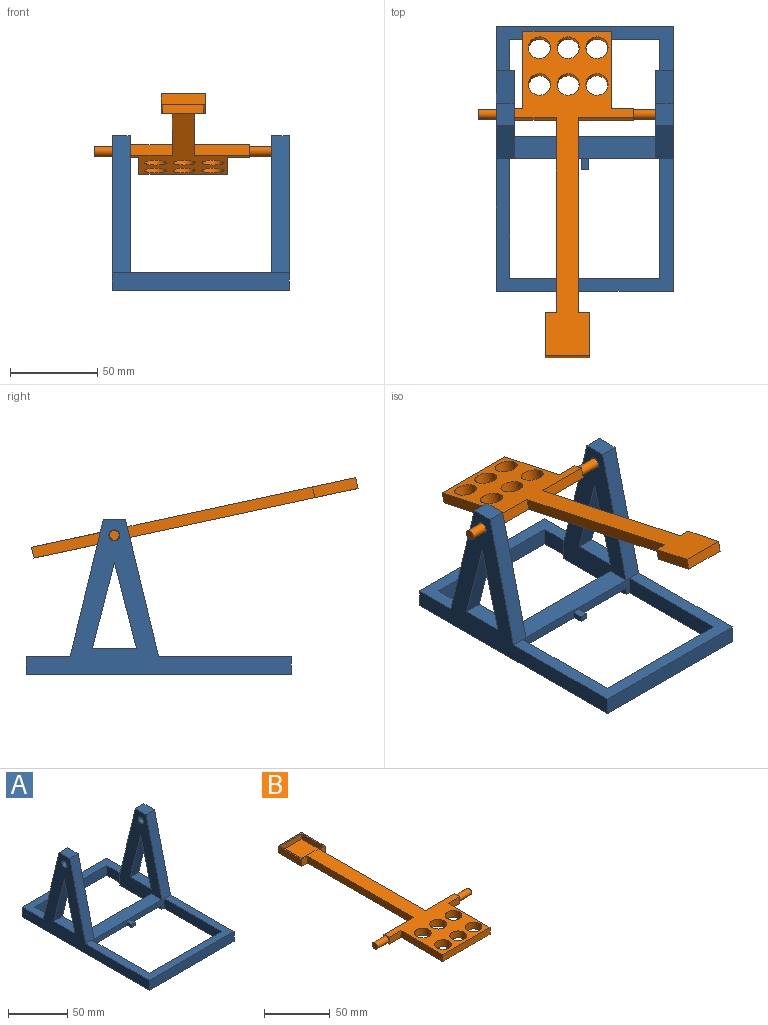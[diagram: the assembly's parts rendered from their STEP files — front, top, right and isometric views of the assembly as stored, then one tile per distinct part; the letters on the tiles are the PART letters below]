
ASSEMBLY  parts=2 mates=1
PART A: 40 faces, bbox 101.6x152.4x88.9 mm
  f0: plane 88.9x50.8mm, normal (-1,0,0), area 2281.3mm2, adj f2,f4,f13,f19,f26,f27,f28,f29
  f1: plane 12.7x10.16mm, normal (0,0,1), area 129mm2, adj f5,f7,f24,f25
  f2: plane 12.7x10.16mm, normal (0,0,1), area 129mm2, adj f0,f6,f30,f31
  f3: plane 10.16x2.54mm, normal (0,1,0), area 25.8mm2, adj f7,f10,f19,f24
  f4: plane 86.36x10.16mm, normal (0,-1,0), area 495.1mm2, adj f0,f7,f14,f16,f19,f25,f31,f32
  f5: plane 152.4x88.9mm, normal (-1,0,0), area 3385.4mm2, adj f1,f8,f9,f17,f18,f19,f20,f21
  f6: plane 152.4x88.9mm, normal (1,0,0), area 3385.4mm2, adj f2,f8,f9,f17,f18,f19,f26,f27
  f7: plane 88.9x50.8mm, normal (1,0,0), area 2281.3mm2, adj f1,f3,f4,f19,f20,f21,f22,f23
  f8: plane 101.6x25.4mm, normal (0,0,1), area 1045.2mm2, adj f5,f6,f10,f11,f12,f17,f24,f30
  f9: plane 101.6x10.16mm, normal (0,-1,0), area 1032.3mm2, adj f5,f6,f18,f19
  f10: plane 17.78x10.16mm, normal (1,0,0), area 180.6mm2, adj f3,f8,f11,f19
  f11: plane 86.36x10.16mm, normal (0,-1,0), area 877.4mm2, adj f8,f10,f12,f19
  f12: plane 17.78x10.16mm, normal (-1,0,0), area 180.6mm2, adj f8,f11,f13,f19
  f13: plane 10.16x2.54mm, normal (0,1,0), area 25.8mm2, adj f0,f12,f19,f30
  f14: plane 68.58x10.16mm, normal (-1,0,0), area 696.8mm2, adj f4,f15,f18,f19
  f15: plane 86.36x10.16mm, normal (0,1,0), area 877.4mm2, adj f14,f16,f18,f19
  f16: plane 68.58x10.16mm, normal (1,0,0), area 696.8mm2, adj f4,f15,f18,f19
  f17: plane 101.6x10.16mm, normal (0,1,0), area 1032.3mm2, adj f5,f6,f8,f19
  f18: plane 101.6x76.2mm, normal (0,0,1), area 1819.4mm2, adj f5,f6,f9,f14,f15,f16,f25,f31
  f19: plane 152.4x101.6mm, normal (0,0,-1), area 3896.8mm2, adj f0,f3,f4,f5,f6,f7,f9,f10
  f20: cylinder r=3.17mm len=10.16mm, axis (1,0,0), area 202.7mm2, adj f5,f7
  f21: plane 25.4x10.16mm, normal (0,0,1), area 258.1mm2, adj f5,f7,f22,f23
  f22: plane 49.71x12.7mm, normal (0,0.97,-0.25), area 521.3mm2, adj f5,f7,f21,f23
  f23: plane 49.71x12.7mm, normal (0,-0.97,-0.25), area 521.3mm2, adj f5,f7,f21,f22
  f24: plane 78.74x19.05mm, normal (0,0.97,0.24), area 823.1mm2, adj f1,f3,f5,f7,f8
  f25: plane 78.74x19.05mm, normal (0,-0.97,0.24), area 823.1mm2, adj f1,f4,f5,f7,f18
  f26: cylinder r=3.17mm len=10.16mm, axis (1,0,0), area 202.7mm2, adj f0,f6
  f27: plane 25.4x10.16mm, normal (0,0,1), area 258.1mm2, adj f0,f6,f28,f29
  f28: plane 49.71x12.7mm, normal (0,0.97,-0.25), area 521.3mm2, adj f0,f6,f27,f29
  f29: plane 49.71x12.7mm, normal (0,-0.97,-0.25), area 521.3mm2, adj f0,f6,f27,f28
  f30: plane 78.74x19.05mm, normal (0,0.97,0.24), area 823.1mm2, adj f0,f2,f6,f8,f13
  f31: plane 78.74x19.05mm, normal (0,-0.97,0.24), area 823.1mm2, adj f0,f2,f4,f6,f18
  f32: plane 81.28x12.75mm, normal (0,0,1), area 1036.4mm2, adj f0,f4,f7,f33
  f33: plane 81.28x5.63mm, normal (0,1,0), area 457.9mm2, adj f0,f7,f32,f34
  f34: plane 81.28x12.75mm, normal (0,0,-1), area 1036.4mm2, adj f0,f4,f7,f33
  f35: plane 6.35x4.41mm, normal (0,0,-1), area 28mm2, adj f4,f36,f38,f39
  f36: plane 6.35x3.26mm, normal (1,0,0), area 20.7mm2, adj f4,f35,f37,f39
  f37: plane 6.35x4.41mm, normal (0,0,1), area 28mm2, adj f4,f36,f38,f39
  f38: plane 6.35x3.26mm, normal (-1,0,0), area 20.7mm2, adj f4,f35,f37,f39
  f39: plane 4.41x3.26mm, normal (0,-1,0), area 14.4mm2, adj f35,f36,f37,f38
PART B: 35 faces, bbox 101.6x190.5x6.4 mm
  f0: plane 45.21x6.35mm, normal (-1,0,0), area 287.1mm2, adj f2,f12,f14,f29
  f1: cylinder r=2.79mm len=12.7mm, axis (1,0,0), area 223mm2, adj f17,f30,f31
  f2: plane 190.5x76.2mm, normal (0,0,1), area 3513.2mm2, adj f0,f3,f4,f5,f6,f7,f8,f9
  f3: plane 31.75x6.35mm, normal (0,1,0), area 201.6mm2, adj f2,f4,f14,f33,f34
  f4: plane 114.3x6.35mm, normal (1,0,0), area 725.8mm2, adj f2,f3,f5,f14
  f5: plane 6.35x6.35mm, normal (0,-1,0), area 40.3mm2, adj f2,f4,f6,f14
  f6: plane 25.4x6.35mm, normal (1,0,0), area 161.3mm2, adj f2,f5,f7,f14
  f7: plane 25.4x6.35mm, normal (0,1,0), area 161.3mm2, adj f2,f6,f8,f14
  f8: plane 25.4x6.35mm, normal (-1,0,0), area 161.3mm2, adj f2,f7,f9,f14
  f9: plane 6.35x6.35mm, normal (0,-1,0), area 40.3mm2, adj f2,f8,f10,f14
  f10: plane 114.3x6.35mm, normal (-1,0,0), area 725.8mm2, adj f2,f9,f11,f14
  f11: plane 31.75x6.35mm, normal (0,1,0), area 201.6mm2, adj f2,f10,f14,f30,f31
  f12: plane 50.8x6.35mm, normal (0,-1,0), area 322.6mm2, adj f0,f2,f13,f14
  f13: plane 45.21x6.35mm, normal (1,0,0), area 287.1mm2, adj f2,f12,f14,f32
  f14: plane 190.5x76.2mm, normal (0,0,-1), area 4059.3mm2, adj f0,f3,f4,f5,f6,f7,f8,f9
  f15: plane 5.59x5.59mm, normal (1,0,0), area 24.5mm2, adj f16
  f16: cylinder r=2.79mm len=12.7mm, axis (1,0,0), area 223mm2, adj f15,f33,f34
  f17: plane 5.59x5.59mm, normal (-1,0,0), area 24.5mm2, adj f1
  f18: plane 23.37x5.08mm, normal (0,-1,0), area 118.7mm2, adj f2,f19,f21,f22
  f19: plane 23.37x5.08mm, normal (1,0,0), area 118.7mm2, adj f2,f18,f20,f22
  f20: plane 23.37x5.08mm, normal (0,1,0), area 118.7mm2, adj f2,f19,f21,f22
  f21: plane 23.37x5.08mm, normal (-1,0,0), area 118.7mm2, adj f2,f18,f20,f22
  f22: plane 23.37x23.37mm, normal (0,0,1), area 546.1mm2, adj f18,f19,f20,f21
  f23: cylinder r=6.35mm len=12.7mm, axis (0,0,1), area 253.4mm2, adj f2,f14
  f24: cylinder r=6.35mm len=12.7mm, axis (0,0,1), area 253.4mm2, adj f2,f14
  f25: cylinder r=6.35mm len=12.7mm, axis (0,0,1), area 253.4mm2, adj f2,f14
  f26: cylinder r=6.35mm len=12.7mm, axis (0,0,1), area 253.4mm2, adj f2,f14
  f27: cylinder r=6.35mm len=12.7mm, axis (0,0,1), area 253.4mm2, adj f2,f14
  f28: cylinder r=6.35mm len=12.7mm, axis (0,0,1), area 253.4mm2, adj f2,f14
  f29: plane 12.7x6.35mm, normal (0,-1,0), area 80.6mm2, adj f0,f2,f14,f30,f31
  f30: plane 5.59x3.05mm, normal (-1,0,0), area 4.8mm2, adj f1,f2,f11,f29
  f31: plane 5.59x3.3mm, normal (-1,0,0), area 6.2mm2, adj f1,f11,f14,f29
  f32: plane 12.7x6.35mm, normal (0,-1,0), area 80.6mm2, adj f2,f13,f14,f33,f34
  f33: plane 5.59x3.05mm, normal (1,0,0), area 4.8mm2, adj f2,f3,f16,f32
  f34: plane 5.59x3.3mm, normal (1,0,0), area 6.2mm2, adj f3,f14,f16,f32
PLACE A t=(-3.38,1.47,26.42)mm fixed
PLACE B rot(axis=(1,0,0),167.9deg) t=(-20.72,45.97,104.79)mm
MATE revolute B.f1 <-> A.f20  axis (1,0,0) through (30.08,23.18,106.31)mm
